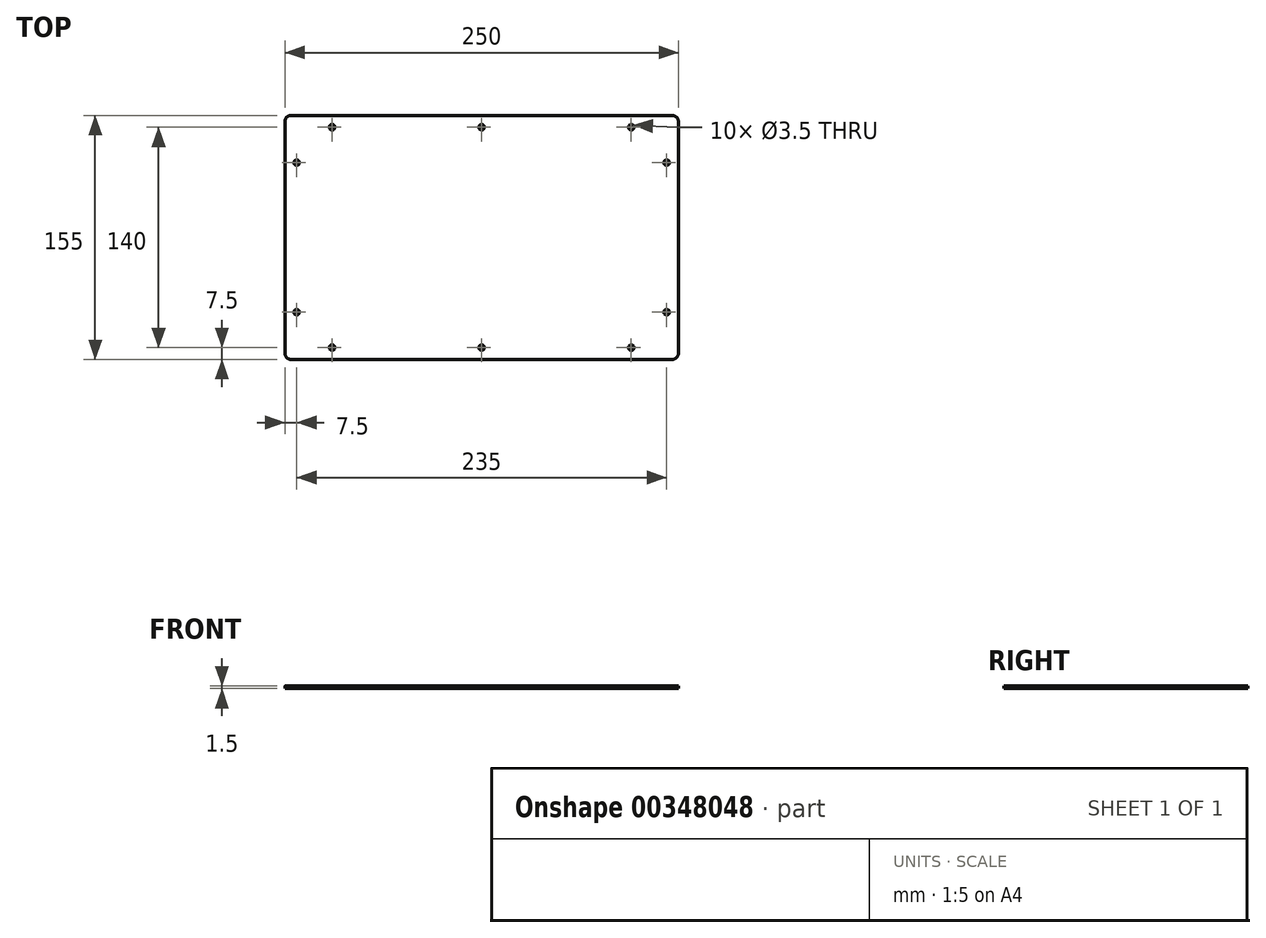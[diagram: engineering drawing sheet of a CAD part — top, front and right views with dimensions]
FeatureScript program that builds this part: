
annotation { "Feature Type Name" : "Feature", "Feature Type Description" : "" }
export const myFeature = defineFeature(function(context is Context, id is Id, definition is map)
    precondition{}
    {
        {
            var Q0;
            Q0=qCreatedBy(makeId("Top.planeOp"),FACE);
            var sketch = newSketch(context, id + "F0", { "sketchPlane" : qUnion([Q0])});
            skLineSegment(sketch, "E0.bottom", {"start": v(-121, 77.5) * mm, "end": v(121, 77.5) * mm});
            skLineSegment(sketch, "E0.top", {"start": v(-121, -77.5) * mm, "end": v(121, -77.5) * mm});
            skLineSegment(sketch, "E0.left", {"start": v(-125, 73.5) * mm, "end": v(-125, -73.5) * mm});
            skLineSegment(sketch, "E0.right", {"start": v(125, 73.5) * mm, "end": v(125, -73.5) * mm});
            skPoint(sketch, "E0.middle", {"position": v(0, 0) * mm});
            skPoint(sketch, "E1.visualSharp", {"position": v(-125, 77.5) * mm});
            skArc(sketch, "E1.filletArc", {"start": v(-121, 77.5) * mm, "mid": v(-123.83, 76.33) * mm, "end": v(-125, 73.5) * mm});
            skPoint(sketch, "E2.visualSharp", {"position": v(-125, -77.5) * mm});
            skArc(sketch, "E2.filletArc", {"start": v(-125, -73.5) * mm, "mid": v(-123.83, -76.33) * mm, "end": v(-121, -77.5) * mm});
            skPoint(sketch, "E3.visualSharp", {"position": v(125, 77.5) * mm});
            skArc(sketch, "E3.filletArc", {"start": v(125, 73.5) * mm, "mid": v(123.83, 76.33) * mm, "end": v(121, 77.5) * mm});
            skPoint(sketch, "E4.visualSharp", {"position": v(125, -77.5) * mm});
            skArc(sketch, "E4.filletArc", {"start": v(121, -77.5) * mm, "mid": v(123.83, -76.33) * mm, "end": v(125, -73.5) * mm});
            skCircle(sketch, "E5", {"center": v(-95, 70) * mm, "radius": 1.75 * mm});
            skLineSegment(sketch, "E6", {"start": v(-95, 70) * mm, "end": v(-125, 70) * mm, "construction": true});
            skCircle(sketch, "E7.MirrorC", {"center": v(95, 70) * mm, "radius": 1.75 * mm});
            skCircle(sketch, "E8", {"center": v(0, 70) * mm, "radius": 1.75 * mm});
            skCircle(sketch, "E9.MirrorC", {"center": v(0, -70) * mm, "radius": 1.75 * mm});
            skCircle(sketch, "E10.MirrorC", {"center": v(95, -70) * mm, "radius": 1.75 * mm});
            skCircle(sketch, "E11.MirrorC", {"center": v(-95, -70) * mm, "radius": 1.75 * mm});
            skCircle(sketch, "E12", {"center": v(-117.5, -47.5) * mm, "radius": 1.75 * mm});
            skCircle(sketch, "E13.MirrorC", {"center": v(-117.5, 47.5) * mm, "radius": 1.75 * mm});
            skCircle(sketch, "E14.MirrorC", {"center": v(117.5, -47.5) * mm, "radius": 1.75 * mm});
            skCircle(sketch, "E15.MirrorC", {"center": v(117.5, 47.5) * mm, "radius": 1.75 * mm});
            skSolve(sketch);
        }
        {
            var Q0;
            Q0=makeQuery(id+"F0.imprint","IMPRINT",FACE,{"disambiguationData":[TD([[makeQuery(id+"F0.imprint","IMPRINT",EDGE,{"derivedFrom":sQuery(id+"F0.wireOp",EDGE,"E0.bottom")}),-1.0]])]});
            extrude(context, id + "F1", {"entities" : qUnion([Q0]), "depth" : 1.5 * mm});
        }
    });
